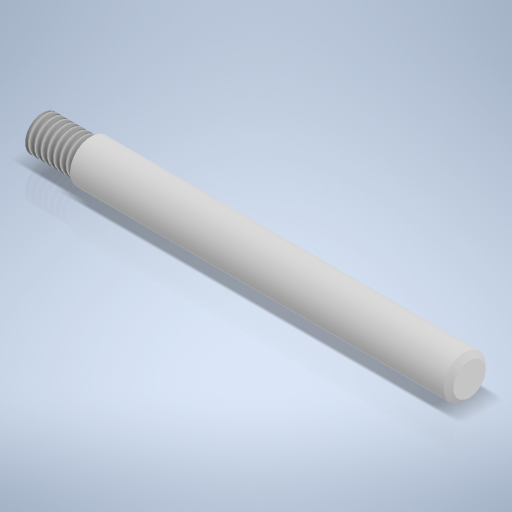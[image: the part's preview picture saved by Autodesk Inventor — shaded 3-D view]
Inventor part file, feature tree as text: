
AUTODESK INVENTOR PART (.ipt)
format: ipt  version: 2024 (Build 280153000, 153)  size: 255,488 bytes
history: native  units: mm
features: revolve x1, thread x1, chamfer x1, sketch x1
ambient origin geometry x8: Origin, YZ Plane, XZ Plane, XY Plane, X Axis, Y Axis, Z Axis, Center Point
bodies: Body1 (feature_tree)
feature tree (4):
  revolve  "Umdrehung2"
  thread  "Gewinde2"  [1 undecoded]
  chamfer  "Fasen1"  Distance=2.5mm
  sketch  "Skizze4"  dims[d12=3.0mm d13=2.5mm d14=90.0deg d15=4.0mm d16=0.0mm d17=0.35mm d18=2.0mm d19=45.0deg]
note: 1 required parameter value undecoded (feature->parameter linkage not recoverable at this tier; creation-order binding heuristic only, values carry confidence <= 0.55)
